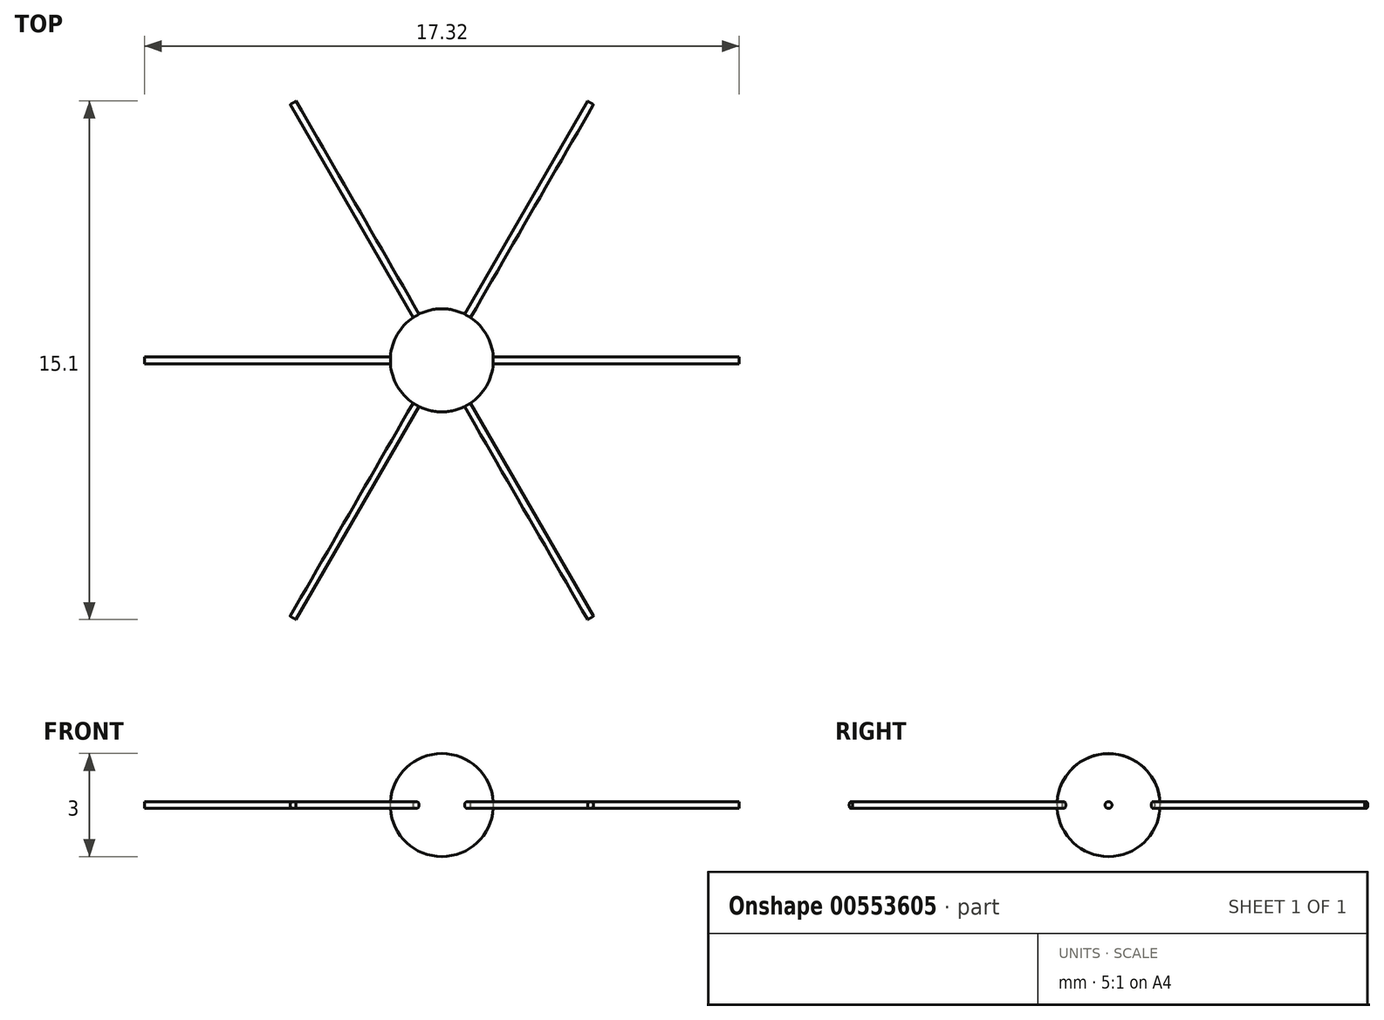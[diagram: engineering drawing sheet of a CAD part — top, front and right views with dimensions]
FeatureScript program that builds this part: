
annotation { "Feature Type Name" : "Feature", "Feature Type Description" : "" }
export const myFeature = defineFeature(function(context is Context, id is Id, definition is map)
    precondition{}
    {
        {
            var Q0;
            Q0=qCreatedBy(makeId("Top.planeOp"),FACE);
            var sketch = newSketch(context, id + "F0", { "sketchPlane" : qUnion([Q0])});
            skArc(sketch, "E0", {"start": v(0, -1.5) * mm, "mid": v(1.5, 0) * mm, "end": v(0, 1.5) * mm});
            skLineSegment(sketch, "E1", {"start": v(0, 1.5) * mm, "end": v(0, -1.5) * mm});
            skSolve(sketch);
        }
        {
            var Q0;
            Q0=qSketchRegion(id+"F0",true);
            var Q1;
            Q1=sQuery(id+"F0.wireOp",EDGE,"E1");
            revolve(context, id + "F1", {"entities" : qUnion([Q0]), "axis" : qUnion([Q1]), "revolveType" : RevolveType.FULL});
        }
        {
            var Q0;
            Q0=qCreatedBy(makeId("Top.planeOp"),FACE);
            var sketch = newSketch(context, id + "F2", { "sketchPlane" : qUnion([Q0])});
            skCircle(sketch, "E2.cCircle", {"center": v(0, 0) * mm, "radius": 7.5 * mm, "construction": true});
            skLineSegment(sketch, "E2.0", {"start": v(4.33, 7.5) * mm, "end": v(8.66, 0) * mm});
            skLineSegment(sketch, "E2.1", {"start": v(8.66, 0) * mm, "end": v(4.33, -7.5) * mm});
            skLineSegment(sketch, "E2.2", {"start": v(4.33, -7.5) * mm, "end": v(-4.33, -7.5) * mm});
            skLineSegment(sketch, "E2.3", {"start": v(-4.33, -7.5) * mm, "end": v(-8.66, 0) * mm});
            skLineSegment(sketch, "E2.4", {"start": v(-8.66, 0) * mm, "end": v(-4.33, 7.5) * mm});
            skLineSegment(sketch, "E2.5", {"start": v(-4.33, 7.5) * mm, "end": v(4.33, 7.5) * mm});
            skPoint(sketch, "E2.0.midPoint", {"position": v(6.5, 3.75) * mm});
            skLineSegment(sketch, "E3", {"start": v(0, 0) * mm, "end": v(4.33, 7.5) * mm});
            skLineSegment(sketch, "E4", {"start": v(0, 0) * mm, "end": v(-4.33, 7.5) * mm});
            skLineSegment(sketch, "E5", {"start": v(0, 0) * mm, "end": v(-8.66, 0) * mm});
            skLineSegment(sketch, "E6", {"start": v(0, 0) * mm, "end": v(-4.33, -7.5) * mm});
            skLineSegment(sketch, "E7", {"start": v(0, 0) * mm, "end": v(4.33, -7.5) * mm});
            skLineSegment(sketch, "E8", {"start": v(0, 0) * mm, "end": v(8.66, 0) * mm});
            skSolve(sketch);
        }
        {
            var Q0;
            Q0=sQuery(id+"F2.wireOp",VERTEX,"E2.3.start");
            var Q1;
            Q1=sQuery(id+"F2.wireOp",EDGE,"E6");
            cPlane(context, id + "F3", {"entities" : qUnion([Q0, Q1]), "cplaneType" : CPlaneType.LINE_POINT, "offset" : 25 * mm, "width" : 150 * mm, "height" : 150 * mm});
        }
        {
            var Q0;
            Q0=sQuery(id+"F2.wireOp",VERTEX,"E5.end");
            var Q1;
            Q1=sQuery(id+"F2.wireOp",EDGE,"E5");
            cPlane(context, id + "F4", {"entities" : qUnion([Q0, Q1]), "cplaneType" : CPlaneType.LINE_POINT, "offset" : 25 * mm, "width" : 150 * mm, "height" : 150 * mm});
        }
        {
            var Q0;
            Q0=sQuery(id+"F2.wireOp",VERTEX,"E4.end");
            var Q1;
            Q1=sQuery(id+"F2.wireOp",EDGE,"E4");
            cPlane(context, id + "F5", {"entities" : qUnion([Q0, Q1]), "cplaneType" : CPlaneType.LINE_POINT, "offset" : 25 * mm, "width" : 150 * mm, "height" : 150 * mm});
        }
        {
            var Q0;
            Q0=qCreatedBy(id+"F3.planeOp",FACE);
            var sketch = newSketch(context, id + "F6", { "sketchPlane" : qUnion([Q0])});
            skCircle(sketch, "E9", {"center": v(0, 0) * mm, "radius": 0.1 * mm});
            skSolve(sketch);
        }
        {
            var Q0;
            Q0=qCreatedBy(id+"F4.planeOp",FACE);
            var sketch = newSketch(context, id + "F7", { "sketchPlane" : qUnion([Q0])});
            skCircle(sketch, "E10", {"center": v(0, 0) * mm, "radius": 0.1 * mm});
            skSolve(sketch);
        }
        {
            var Q0;
            Q0=qCreatedBy(id+"F5.planeOp",FACE);
            var sketch = newSketch(context, id + "F8", { "sketchPlane" : qUnion([Q0])});
            skCircle(sketch, "E11", {"center": v(0, 0) * mm, "radius": 0.1 * mm});
            skSolve(sketch);
        }
        {
            var Q0;
            Q0=makeQuery(id+"F8.imprint","IMPRINT",FACE,{"disambiguationData":[TD([[makeQuery(id+"F8.imprint","IMPRINT",EDGE,{"derivedFrom":sQuery(id+"F8.wireOp",EDGE,"E11")}),1.0]])]});
            var Q1;
            Q1=sQuery(id+"F2.wireOp",EDGE,"E4");
            var Q2;
            Q2=sQuery(id+"F2.wireOp",EDGE,"E7");
            sweep(context, id + "F9", {"operationType" : NewBodyOperationType.ADD, "profiles" : qUnion([Q0]), "path" : qUnion([Q1, Q2])});
        }
        {
            var Q0;
            Q0=makeQuery(id+"F7.imprint","IMPRINT",FACE,{"disambiguationData":[TD([[makeQuery(id+"F7.imprint","IMPRINT",EDGE,{"derivedFrom":sQuery(id+"F7.wireOp",EDGE,"E10")}),1.0]])]});
            var Q1;
            Q1=sQuery(id+"F2.wireOp",EDGE,"E5");
            var Q2;
            Q2=sQuery(id+"F2.wireOp",EDGE,"E8");
            sweep(context, id + "F10", {"operationType" : NewBodyOperationType.ADD, "profiles" : qUnion([Q0]), "path" : qUnion([Q1, Q2])});
        }
        {
            var Q0;
            Q0=makeQuery(id+"F6.imprint","IMPRINT",FACE,{"disambiguationData":[TD([[makeQuery(id+"F6.imprint","IMPRINT",EDGE,{"derivedFrom":sQuery(id+"F6.wireOp",EDGE,"E9")}),1.0]])]});
            var Q1;
            Q1=sQuery(id+"F2.wireOp",EDGE,"E6");
            var Q2;
            Q2=sQuery(id+"F2.wireOp",EDGE,"E3");
            sweep(context, id + "F11", {"operationType" : NewBodyOperationType.ADD, "profiles" : qUnion([Q0]), "path" : qUnion([Q1, Q2])});
        }
    });
